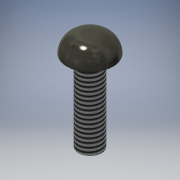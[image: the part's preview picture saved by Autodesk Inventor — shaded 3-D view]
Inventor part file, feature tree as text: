
AUTODESK INVENTOR PART (.ipt)
format: ipt  version: 2016 (Build 200138000, 138)  size: 139,776 bytes
history: native  units: mm
features: extrude x3, sketch x3, other x1, fillet x1, thread x1
ambient origin geometry x1: Origin
bodies: Body1 (feature_tree)
feature tree (9):
  other  "ソリッド1"
  extrude  "押し出し1"  Depth=4.0mm
  extrude  "押し出し2"  Depth=6.0mm TaperAngle=0.0deg
  fillet  "フィレット1"  Radius=8.0mm
  thread  "ねじ1"
  extrude  "押し出し3"  Depth=3.0mm TaperAngle=0.0deg
  sketch  "スケッチ1"
  sketch  "スケッチ2"
  sketch  "スケッチ3"
